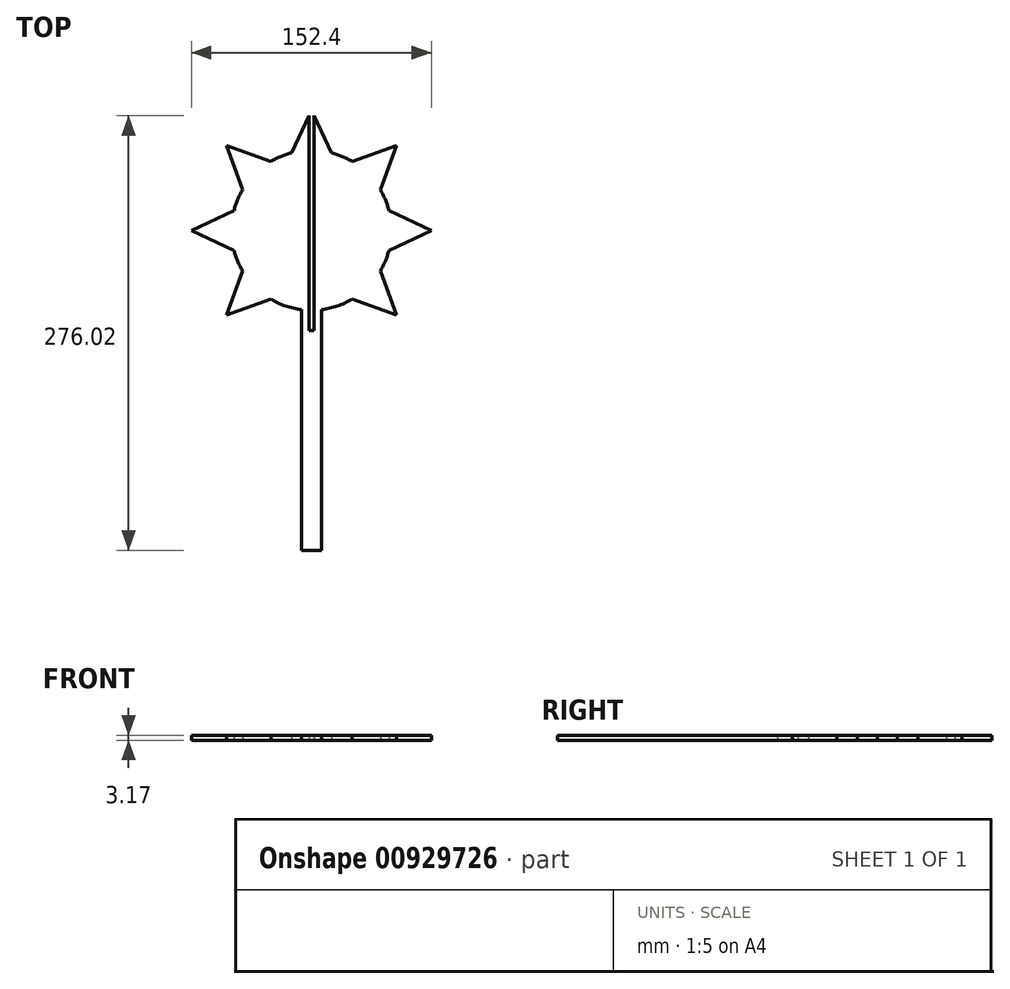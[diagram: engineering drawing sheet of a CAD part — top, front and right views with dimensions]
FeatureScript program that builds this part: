
annotation { "Feature Type Name" : "Feature", "Feature Type Description" : "" }
export const myFeature = defineFeature(function(context is Context, id is Id, definition is map)
    precondition{}
    {
        {
            var Q0;
            Q0=qCreatedBy(makeId("Top.planeOp"),FACE);
            var sketch = newSketch(context, id + "F0", { "sketchPlane" : qUnion([Q0])});
            skLineSegment(sketch, "E0.bottom", {"start": v(-6.35, -101.6) * mm, "end": v(-1.59, -101.6) * mm});
            skLineSegment(sketch, "E0.left", {"start": v(-6.35, -101.6) * mm, "end": v(-6.35, 51.2) * mm});
            skLineSegment(sketch, "E0.right", {"start": v(6.35, -101.6) * mm, "end": v(6.35, 51.2) * mm});
            skPoint(sketch, "E0.middle", {"position": v(0, 0) * mm});
            skArc(sketch, "E1", {"start": v(6.35, 51.2) * mm, "mid": v(16.41, 53.52) * mm, "end": v(25.8, 57.84) * mm});
            skLineSegment(sketch, "E2", {"start": v(-49.19, 88.9) * mm, "end": v(-76.2, 101.6) * mm});
            skLineSegment(sketch, "E3", {"start": v(-76.2, 101.6) * mm, "end": v(-49.19, 114.3) * mm});
            skLineSegment(sketch, "E4", {"start": v(49.19, 114.3) * mm, "end": v(76.2, 101.6) * mm});
            skLineSegment(sketch, "E5", {"start": v(76.2, 101.6) * mm, "end": v(49.19, 88.9) * mm});
            skLineSegment(sketch, "E6", {"start": v(12.7, 150.79) * mm, "end": v(1.59, 174.42) * mm});
            skLineSegment(sketch, "E7", {"start": v(-1.59, 174.42) * mm, "end": v(-12.7, 150.79) * mm});
            skLineSegment(sketch, "E8", {"start": v(-25.8, 145.36) * mm, "end": v(-53.88, 155.48) * mm});
            skLineSegment(sketch, "E9", {"start": v(-53.88, 155.48) * mm, "end": v(-43.76, 127.4) * mm});
            skLineSegment(sketch, "E10", {"start": v(43.76, 127.4) * mm, "end": v(53.88, 155.48) * mm});
            skLineSegment(sketch, "E11", {"start": v(53.88, 155.48) * mm, "end": v(25.8, 145.36) * mm});
            skPoint(sketch, "E12.orphan", {"position": v(6.35, 101.6) * mm});
            skPoint(sketch, "E0.top.start.orphan", {"position": v(-6.35, 101.6) * mm});
            skArc(sketch, "E13.trimOffspring", {"start": v(-49.19, 88.9) * mm, "mid": v(-46.93, 82.16) * mm, "end": v(-43.76, 75.8) * mm});
            skArc(sketch, "E14.trimOffspring", {"start": v(-43.76, 127.4) * mm, "mid": v(-46.93, 121.04) * mm, "end": v(-49.19, 114.3) * mm});
            skArc(sketch, "E15.trimOffspring", {"start": v(-12.7, 150.79) * mm, "mid": v(-19.44, 148.53) * mm, "end": v(-25.8, 145.36) * mm});
            skArc(sketch, "E16.trimOffspring", {"start": v(25.8, 145.36) * mm, "mid": v(19.44, 148.53) * mm, "end": v(12.7, 150.79) * mm});
            skArc(sketch, "E17.trimOffspring", {"start": v(49.19, 114.3) * mm, "mid": v(46.93, 121.04) * mm, "end": v(43.76, 127.4) * mm});
            skLineSegment(sketch, "E18", {"start": v(-43.76, 75.8) * mm, "end": v(-53.88, 47.72) * mm});
            skLineSegment(sketch, "E19", {"start": v(-53.88, 47.72) * mm, "end": v(-25.8, 57.84) * mm});
            skLineSegment(sketch, "E20", {"start": v(43.76, 75.8) * mm, "end": v(53.88, 47.72) * mm});
            skLineSegment(sketch, "E21", {"start": v(53.88, 47.72) * mm, "end": v(25.8, 57.84) * mm});
            skArc(sketch, "E22.trimOffspring", {"start": v(-25.8, 57.84) * mm, "mid": v(-16.41, 53.52) * mm, "end": v(-6.35, 51.2) * mm});
            skArc(sketch, "E23.trimOffspring", {"start": v(43.76, 75.8) * mm, "mid": v(46.93, 82.16) * mm, "end": v(49.19, 88.9) * mm});
            skLineSegment(sketch, "E24.top", {"start": v(-1.59, 38.1) * mm, "end": v(1.59, 38.1) * mm});
            skLineSegment(sketch, "E25.trimOffspring", {"start": v(1.59, -101.6) * mm, "end": v(6.35, -101.6) * mm});
            skLineSegment(sketch, "E26.bottom", {"start": v(1.59, 38.1) * mm, "end": v(-1.59, 38.1) * mm});
            skLineSegment(sketch, "E26.left", {"start": v(1.59, 38.1) * mm, "end": v(1.59, 174.42) * mm});
            skLineSegment(sketch, "E26.right", {"start": v(-1.59, 38.1) * mm, "end": v(-1.59, 174.42) * mm});
            skPoint(sketch, "E26.top.start.orphan", {"position": v(0, 177.8) * mm});
            skPoint(sketch, "E27.end.orphan", {"position": v(-1.59, 177.8) * mm});
            skLineSegment(sketch, "E28", {"start": v(1.59, -101.6) * mm, "end": v(-1.59, -101.6) * mm});
            skSolve(sketch);
        }
        {
            var Q0;
            Q0=qSketchRegion(id+"F0",true);
            extrude(context, id + "F1", {"entities" : qUnion([Q0]), "depth" : 3.17 * mm, "offsetDistance" : 25.4 * mm});
        }
    });
